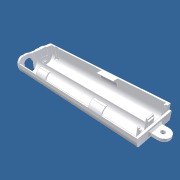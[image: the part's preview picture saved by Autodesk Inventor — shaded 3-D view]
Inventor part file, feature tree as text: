
AUTODESK INVENTOR PART (.ipt)
format: ipt  version: unknown  size: 694,784 bytes
history: native  units: mm
features: extrude x31, sketch x29, plane x3, chamfer x3, other x1, fillet x1, hole x1
ambient origin geometry x8: Origin, YZ Plane, XZ Plane, XY Plane, X Axis, Y Axis, Z Axis, Center Point
bodies: Solid1 (feature_tree)
feature tree (69):
  extrude  "Extrusion1"  Depth=14.5mm
  extrude  "Extrusion2"  Depth=3.0mm
  plane  "Work Plane3"
  other  "Battery Cylinders"
  extrude  "Extrusion5"  Depth=104.5mm TaperAngle=0.0deg
  extrude  "Extrusion6"  Depth=14.5mm
  sketch  "Sketch9"  dims[d5=2.0mm d6=104.5mm d7=0.0mm]
  extrude  "Extrusion8"  Depth=8.75mm
  extrude  "Extrusion9"  Depth=8.5mm TaperAngle=0.0deg
  extrude  "Extrusion11"  Depth=52.2mm
  extrude  "Extrusion12"  Depth=1.5mm
  extrude  "Extrusion13"  Depth=14.1mm
  extrude  "Extrusion15"  Depth=6.0mm
  extrude  "Extrusion16"  Depth=20.2mm
  chamfer  "Chamfer1"  Distance=4.5mm
  extrude  "Extrusion17"  Depth=37.0mm
  plane  "Work Plane4"
  extrude  "Extrusion19"  Depth=2.5mm
  extrude  "Extrusion20"  Depth=60.0mm
  extrude  "Extrusion21"  Depth=1.0mm
  chamfer  "Chamfer2"  Distance=1.5mm
  extrude  "Extrusion22"  Depth=2.0mm TaperAngle=0.0deg
  extrude  "Extrusion23"  Depth=8.0mm
  extrude  "Extrusion24"  Depth=1.0mm
  extrude  "Extrusion25"  Depth=0.7mm TaperAngle=0.0deg
  extrude  "Extrusion26"  Depth=7.0mm TaperAngle=0.0deg
  extrude  "Extrusion27"  Depth=15.0mm
  extrude  "Manufacturing holes"  TaperAngle=0.0deg  [1 undecoded]
  extrude  "Extrusion29"  Depth=4.0mm
  extrude  "Extrusion30"  Depth=5.85mm TaperAngle=0.0deg
  extrude  "Extrusion31"  Depth=3.3mm TaperAngle=0.0deg
  plane  "Work Plane5"
  sketch  "Sketch34"  dims[d86=8.0mm d87=2.0mm d88=0.0mm]
  extrude  "Temporary battery holder"  Depth=0.25mm TaperAngle=45.0deg
  extrude  "+ bat spring notch 1"  Depth=1.0mm
  extrude  "+ bat spring notch 2"  Depth=1.0mm
  extrude  "- bat spring notch"  Depth=0.5mm TaperAngle=0.0deg
  extrude  "Remove more slot material"  Depth=4.0mm
  extrude  "Easy extraction"  Depth=7.0mm
  fillet  "Easy extraction rounded edge"  Radius=10.5mm
  hole  "Easy extraction hole"  [1 undecoded]
  chamfer  "Easy extraction chamfer"  Distance=1.0mm
  sketch  "Sketch1"  dims[d0=31.3mm d1=14.5mm]
  sketch  "Sketch2"  dims[d2=104.5mm d3=0.0mm d4=3.0mm]
  sketch  "Sketch10"  dims[d15=-3.2mm d35=14.5mm]
  sketch  "Sketch11"  dims[d36=14.5mm d37=8.75mm]
  sketch  "Sketch14"  dims[d40=7.85mm d42=8.5mm d43=0.0mm]
  sketch  "Sketch15"  dims[d44=8.5mm d45=0.0mm d52=52.2mm]
  sketch  "Sketch16"  dims[d55=1.5mm d56=1.5mm]
  sketch  "Sketch20"  dims[d57=0.0mm d58=14.1mm]
  sketch  "Sketch21"  dims[d59=6.0mm d60=6.0mm]
  sketch  "Sketch22"  dims[d61=6.75mm d62=0.0mm d63=20.2mm]
  sketch  "Sketch23"  dims[d64=10.0mm]
  sketch  "Sketch24"  dims[d65=39.7mm]
  sketch  "Sketch25"  dims[d66=10.0mm d67=4.5mm d68=0.0mm]
  sketch  "Sketch26"  dims[d71=4.5mm d72=0.0mm d73=37.0mm]
  sketch  "Sketch27"  dims[d74=47.2mm d75=2.5mm]
  sketch  "Sketch28"  dims[d76=2.5mm d77=60.0mm]
  sketch  "Sketch29"  dims[d78=11.5mm d79=1.0mm]
  sketch  "Sketch30"  dims[d80=5.0mm]
  sketch  "Sketch31"  dims[d81=8.0mm]
  sketch  "Sketch33"  dims[d82=10.5mm d83=1.5mm d84=0.0mm]
  sketch  "Sketch35"  dims[d97=10.3mm d98=8.0mm]
  sketch  "Sketch36"  dims[d99=1.0mm d100=0.0mm d101=1.0mm]
  sketch  "Sketch37"  dims[d102=1.0mm d103=0.7mm d104=0.0mm]
  sketch  "Sketch39"  dims[d105=1.0mm d106=1.5mm d107=45.0deg d108=7.0mm d109=0.0mm]
  sketch  "Sketch40"  dims[d121=15.0mm d122=15.0mm]
  sketch  "Sketch41"  dims[d123=1.0mm d124=0.0mm]
  sketch  "Sketch42"  dims[d125=5.85mm d126=0.0mm d127=4.0mm d128=5.85mm d129=0.0mm d130=3.3mm d131=0.0mm d132=0.25mm d133=1.5mm d134=45.0deg d135=1.0mm d136=1.0mm d137=0.5mm d138=0.0mm d139=4.0mm d140=7.0mm d141=10.5mm d142=0.0mm d143=0.75mm d144=1.0mm d145=4.8mm d146=10.5mm d147=0.0mm d148=0.5mm d150=2.5mm d151=1.15mm d152=0.5mm d153=0.0mm d154=0.5mm d155=1.5mm d156=1.5mm d157=1.0mm d158=0.5mm d159=1.0mm d160=3.0mm d161=14.0mm d162=0.0mm d163=2.0mm d164=3.0mm d165=4.5mm d166=1.5mm d167=1.0mm d168=0.0mm d169=2.0mm d170=2.0mm d171=10.0mm d172=10.0mm d173=22.4mm d174=21.4mm d175=3.3mm d176=3.3mm d177=1.5mm d178=0.0mm d179=1.5mm d180=0.0mm d181=0.0mm d182=5.7mm d183=11.0mm d187=1.0mm d188=0.0mm d190=4.0mm d192=4.0mm d193=1.0mm d194=1.5mm d195=1.0mm d196=1.0mm d197=1.0mm d198=1.0mm d199=0.0mm d200=2.0mm d201=1.5mm d202=0.0mm d203=1.0mm d204=4.0mm d205=1.0mm d206=0.0mm d207=1.0mm d208=4.0mm d209=1.0mm d210=0.0mm d212=1.0mm d213=10.0mm d214=0.0mm d215=10.0mm d216=0.0mm d217=10.0mm d218=31.3mm d219=10.65mm d220=2.0mm d221=7.0mm d222=2.5mm d223=10.0mm d224=0.0mm d225=5.0mm d226=3.0mm d227=6.0mm d228=4.0mm d229=2.0mm d230=90.0deg d231=8.0mm d232=0.0mm d233=1.0mm d234=2.0mm d235=45.0deg d236=0.125mm d237=0.125mm]
note: 2 required parameter values undecoded (feature->parameter linkage not recoverable at this tier; creation-order binding heuristic only, values carry confidence <= 0.55)
